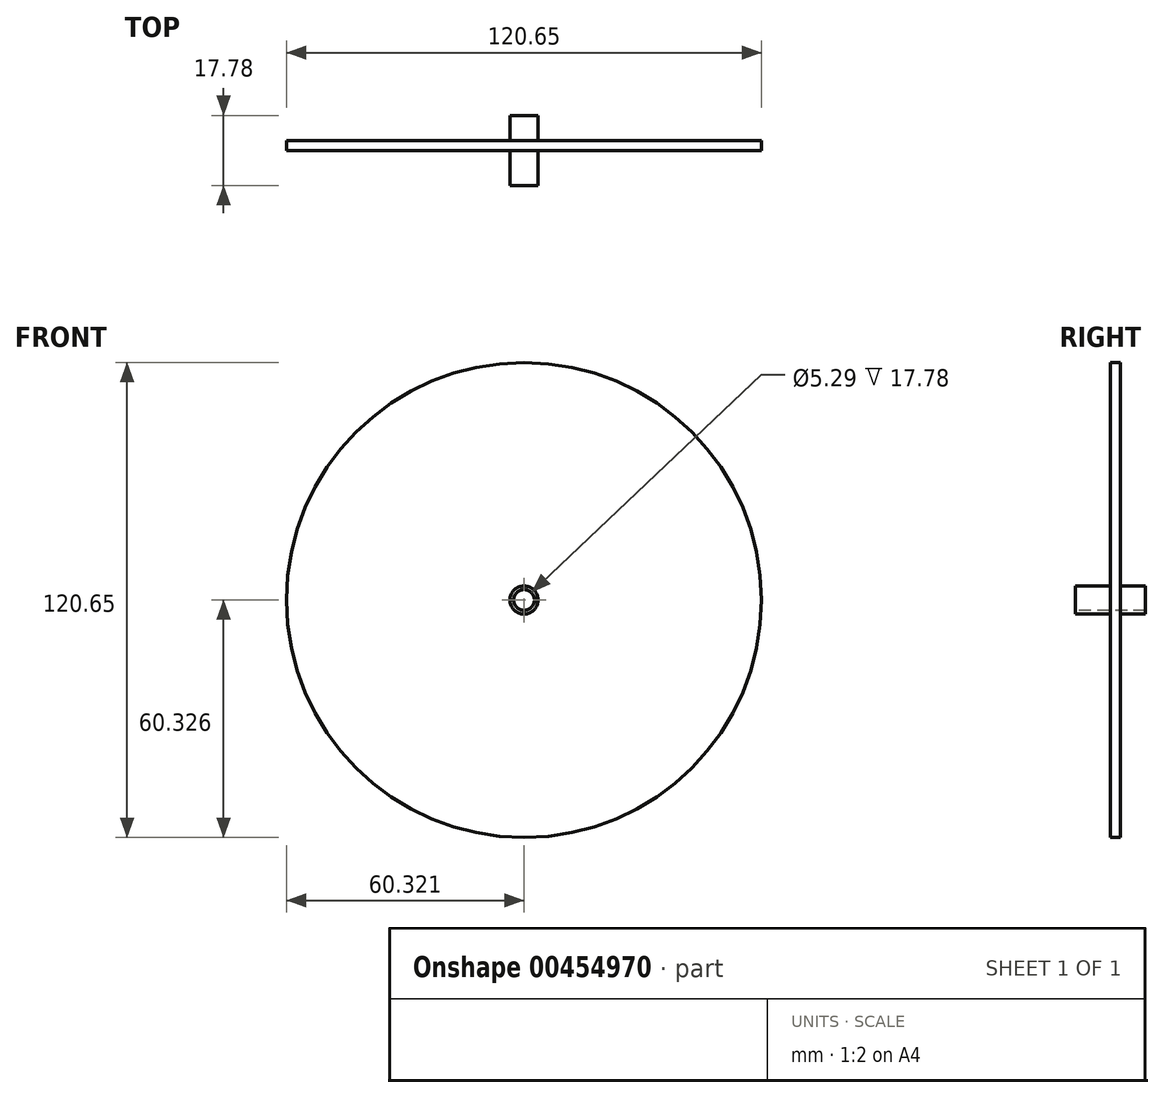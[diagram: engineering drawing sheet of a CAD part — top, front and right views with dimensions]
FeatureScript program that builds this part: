
annotation { "Feature Type Name" : "Feature", "Feature Type Description" : "" }
export const myFeature = defineFeature(function(context is Context, id is Id, definition is map)
    precondition{}
    {
        {
            var Q0;
            Q0=qCreatedBy(makeId("Front.planeOp"),FACE);
            var sketch = newSketch(context, id + "F0", { "sketchPlane" : qUnion([Q0])});
            skCircle(sketch, "E0", {"center": v(-14.84, 8.9) * mm, "radius": 60.32 * mm});
            skSolve(sketch);
        }
        {
            var Q0;
            Q0=makeQuery(id+"F0.imprint","IMPRINT",FACE,{"disambiguationData":[TD([[makeQuery(id+"F0.imprint","IMPRINT",EDGE,{"derivedFrom":sQuery(id+"F0.wireOp",EDGE,"E0")}),1.0]])]});
            extrude(context, id + "F1", {"entities" : qUnion([Q0]), "depth" : 2.54 * mm});
        }
        {
            var Q0;
            Q0=makeQuery(id+"F1.opExtrude","CAP_FACE",FACE,{"disambiguationData":[OSD([sQuery(id+"F0.wireOp",EDGE,"E0")])],"isStart":false});
            var sketch = newSketch(context, id + "F2", { "sketchPlane" : qUnion([Q0])});
            skCircle(sketch, "E1", {"center": v(-14.84, 8.9) * mm, "radius": 3.56 * mm});
            skSolve(sketch);
        }
        {
            var Q0;
            Q0 = qSketchRegion(id + "F2", true);
            var Q1;
            Q1=sQuery(id+"F2.wireOp",EDGE,"E1");
            extrude(context, id + "F3", {"entities" : qUnion([Q0]), "operationType" : NewBodyOperationType.ADD, "surfaceEntities" : qUnion([Q1]), "endBound" : BoundingType.SYMMETRIC, "depth" : 7.62 * mm});
        }
        {
            var Q0;
            Q0=makeQuery(id+"F3.opExtrude","CAP_FACE",FACE,{"disambiguationData":[OSD([sQuery(id+"F2.wireOp",EDGE,"E1")])],"isStart":true});
            extrude(context, id + "F4", {"entities" : qUnion([Q0]), "operationType" : NewBodyOperationType.ADD, "depth" : 5.08 * mm});
        }
        {
            var Q0;
            Q0=makeQuery(id+"F3.opExtrude","CAP_FACE",FACE,{"disambiguationData":[OSD([sQuery(id+"F2.wireOp",EDGE,"E1")])],"isStart":false});
            extrude(context, id + "F5", {"entities" : qUnion([Q0]), "operationType" : NewBodyOperationType.ADD, "depth" : 5.08 * mm});
        }
        {
            var Q0;
            Q0=makeQuery(id+"F5.opExtrude","CAP_FACE",FACE,{"disambiguationData":[OSD([sQuery(id+"F2.wireOp",EDGE,"E1")])],"isStart":false});
            var sketch = newSketch(context, id + "F6", { "sketchPlane" : qUnion([Q0])});
            skCircle(sketch, "E2", {"center": v(-14.84, 8.9) * mm, "radius": 2.64 * mm});
            skSolve(sketch);
        }
        {
            var Q0;
            Q0 = qSketchRegion(id + "F6", true);
            extrude(context, id + "F7", {"entities" : qUnion([Q0]), "operationType" : NewBodyOperationType.REMOVE, "endBound" : BoundingType.THROUGH_ALL, "oppositeDirection" : true, "depth" : 25.4 * mm});
        }
    });
